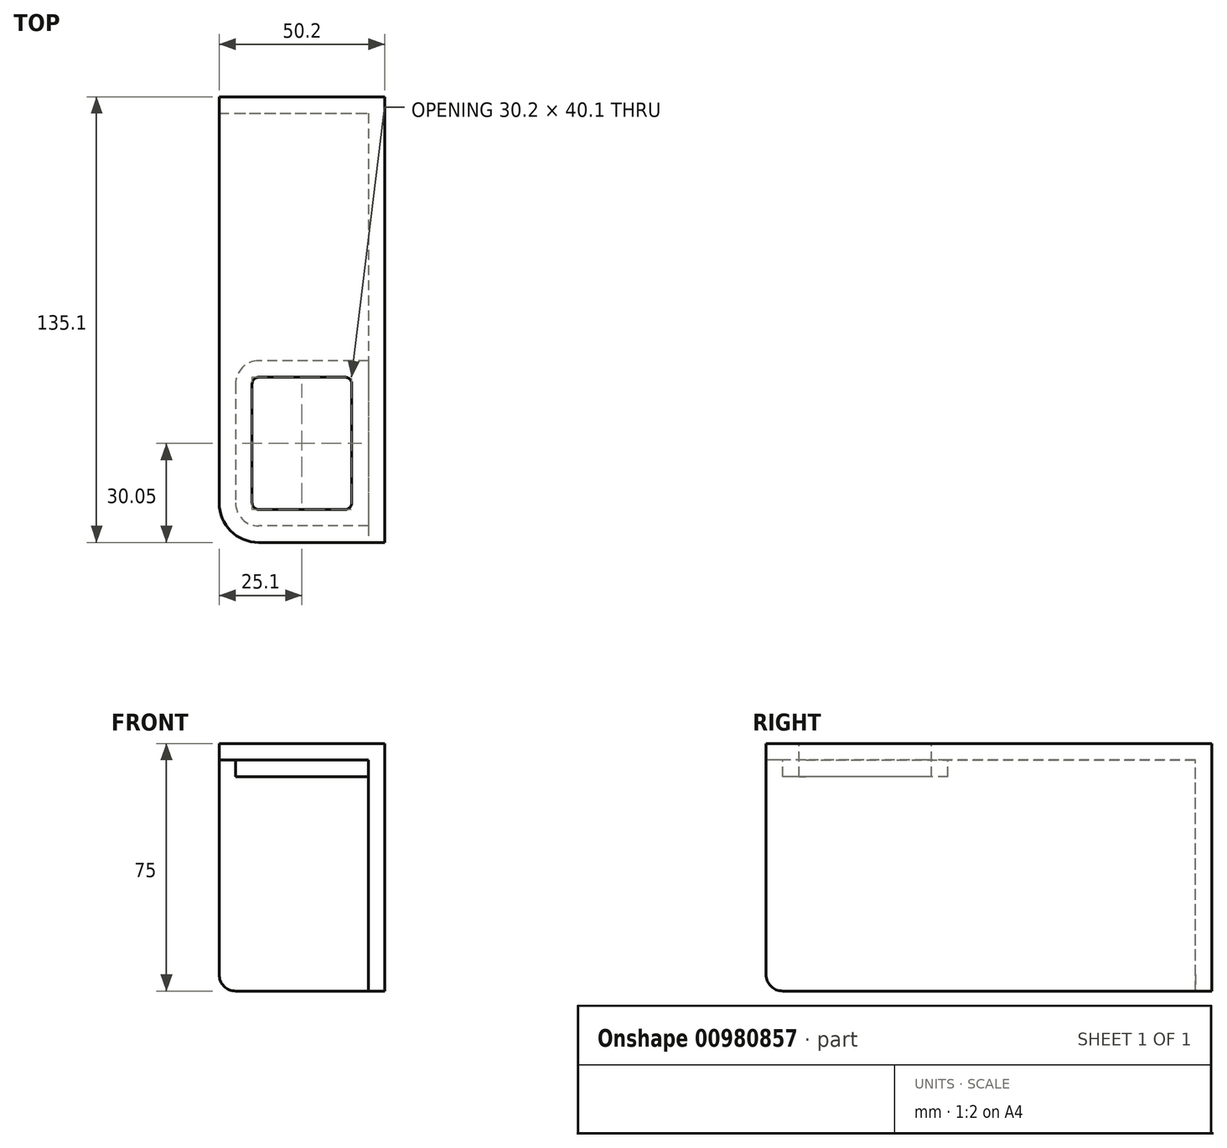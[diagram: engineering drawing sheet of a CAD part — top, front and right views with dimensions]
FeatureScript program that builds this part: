
annotation { "Feature Type Name" : "Feature", "Feature Type Description" : "" }
export const myFeature = defineFeature(function(context is Context, id is Id, definition is map)
    precondition{}
    {
        {
            var Q0;
            Q0=qCreatedBy(makeId("Top.planeOp"),FACE);
            var sketch = newSketch(context, id + "F0", { "sketchPlane" : qUnion([Q0])});
            skLineSegment(sketch, "E0.bottom", {"start": v(13.1, 20.05) * mm, "end": v(-13.1, 20.05) * mm});
            skLineSegment(sketch, "E0.top", {"start": v(13.1, -20.05) * mm, "end": v(-13.1, -20.05) * mm});
            skLineSegment(sketch, "E0.left", {"start": v(15.1, 18.05) * mm, "end": v(15.1, -18.05) * mm});
            skLineSegment(sketch, "E0.right", {"start": v(-15.1, 18.05) * mm, "end": v(-15.1, -18.05) * mm});
            skPoint(sketch, "E0.middle", {"position": v(0, 0) * mm});
            skPoint(sketch, "E1.visualSharp", {"position": v(-15.1, -20.05) * mm});
            skArc(sketch, "E1.filletArc", {"start": v(-15.1, -18.05) * mm, "mid": v(-14.51, -19.46) * mm, "end": v(-13.1, -20.05) * mm});
            skPoint(sketch, "E2.visualSharp", {"position": v(15.1, -20.05) * mm});
            skArc(sketch, "E2.filletArc", {"start": v(13.1, -20.05) * mm, "mid": v(14.51, -19.46) * mm, "end": v(15.1, -18.05) * mm});
            skPoint(sketch, "E3.visualSharp", {"position": v(15.1, 20.05) * mm});
            skArc(sketch, "E3.filletArc", {"start": v(15.1, 18.05) * mm, "mid": v(14.51, 19.46) * mm, "end": v(13.1, 20.05) * mm});
            skPoint(sketch, "E4.visualSharp", {"position": v(-15.1, 20.05) * mm});
            skArc(sketch, "E4.filletArc", {"start": v(-13.1, 20.05) * mm, "mid": v(-14.51, 19.46) * mm, "end": v(-15.1, 18.05) * mm});
            skArc(sketch, "E5.0", {"start": v(-13.1, 25.05) * mm, "mid": v(-18.05, 23) * mm, "end": v(-20.1, 18.05) * mm});
            skLineSegment(sketch, "E5.1", {"start": v(20.1, 25.05) * mm, "end": v(-13.1, 25.05) * mm});
            skLineSegment(sketch, "E5.2", {"start": v(-20.1, 18.05) * mm, "end": v(-20.1, -18.05) * mm});
            skArc(sketch, "E5.4", {"start": v(-20.1, -18.05) * mm, "mid": v(-18.05, -23) * mm, "end": v(-13.1, -25.05) * mm});
            skLineSegment(sketch, "E5.5", {"start": v(20.1, -25.05) * mm, "end": v(-13.1, -25.05) * mm});
            skLineSegment(sketch, "E6", {"start": v(-18.7, 95.35) * mm, "end": v(21.85, 95.35) * mm, "construction": true});
            skLineSegment(sketch, "E7.bottom", {"start": v(-13.1, -30.05) * mm, "end": v(25.1, -30.05) * mm});
            skLineSegment(sketch, "E7.top", {"start": v(-25.1, 105.05) * mm, "end": v(25.1, 105.05) * mm});
            skLineSegment(sketch, "E7.left", {"start": v(-25.1, -18.05) * mm, "end": v(-25.1, 105.05) * mm});
            skLineSegment(sketch, "E7.right", {"start": v(25.1, -30.05) * mm, "end": v(25.1, 105.05) * mm});
            skLineSegment(sketch, "E8", {"start": v(-25.1, 100.05) * mm, "end": v(20.1, 100.05) * mm});
            skLineSegment(sketch, "E9", {"start": v(20.1, 100.05) * mm, "end": v(20.1, -30.05) * mm});
            skPoint(sketch, "E10.visualSharp", {"position": v(-25.1, -30.05) * mm});
            skArc(sketch, "E10.filletArc", {"start": v(-25.1, -18.05) * mm, "mid": v(-21.59, -26.54) * mm, "end": v(-13.1, -30.05) * mm});
            skSolve(sketch);
        }
        {
            var Q0;
            Q0=makeQuery(id+"F0.imprint","IMPRINT",FACE,{"disambiguationData":[TD([[makeQuery(id+"F0.imprint","IMPRINT",EDGE,{"derivedFrom":sQuery(id+"F0.wireOp",EDGE,"E5.0")}),-1.0]])]});
            extrude(context, id + "F1", {"entities" : qUnion([Q0]), "oppositeDirection" : true, "depth" : 5 * mm, "offsetDistance" : 25 * mm});
        }
        {
            var Q0;
            Q0=makeQuery(id+"F0.imprint","IMPRINT",FACE,{"disambiguationData":[TD([[makeQuery(id+"F0.imprint","IMPRINT",EDGE,{"derivedFrom":sQuery(id+"F0.wireOp",EDGE,"E0.bottom")}),-1.0]])]});
            extrude(context, id + "F2", {"entities" : qUnion([Q0]), "operationType" : NewBodyOperationType.ADD, "oppositeDirection" : true, "depth" : 10 * mm, "offsetDistance" : 25 * mm});
        }
        {
            var Q0;
            {var subQ2=sQuery(id+"F0.wireOp",EDGE,"E7.top");Q0=makeQuery(id+"F0.imprint","IMPRINT",FACE,{"disambiguationData":[TD([[makeQuery(id+"F0.imprint","IMPRINT",EDGE,{"derivedFrom":subQ2}),-1.0]])]});}
            extrude(context, id + "F3", {"entities" : qUnion([Q0]), "operationType" : NewBodyOperationType.ADD, "oppositeDirection" : true, "depth" : 75 * mm, "offsetDistance" : 25 * mm});
        }
        {
            var Q0;
            {var subQ0=sQuery(id+"F0.wireOp",EDGE,"E9");Q0=makeQuery(id+"F1.opExtrude","CAP_EDGE",EDGE,{"disambiguationData":[OSD([subQ0]),TDD([makeQuery(id+"F0.imprint","IMPRINT",EDGE,{"disambiguationData":[TD([[makeQuery(id+"F0.imprint","INTERSECT",VERTEX,{"derivedFrom":[sQuery(id+"F0.wireOp",EDGE,"E5.5"),subQ0]}),-1.0]])],"derivedFrom":subQ0})])],"isStart":false});}
            var Q1;
            {var subQ0=sQuery(id+"F0.wireOp",EDGE,"E9");Q1=makeQuery(id+"F1.opExtrude","CAP_EDGE",EDGE,{"disambiguationData":[OSD([subQ0]),TDD([makeQuery(id+"F0.imprint","IMPRINT",EDGE,{"disambiguationData":[TD([[makeQuery(id+"F0.imprint","INTERSECT",VERTEX,{"derivedFrom":[sQuery(id+"F0.wireOp",EDGE,"E5.1"),subQ0]}),1.0]])],"derivedFrom":subQ0})])],"isStart":false});}
            var Q2;
            Q2=makeQuery(id+"F2.opExtrude","CAP_EDGE",EDGE,{"disambiguationData":[OSD([sQuery(id+"F0.wireOp",EDGE,"E9")])],"isStart":false});
            var Q3;
            Q3=makeQuery(id+"F3.opExtrude","CAP_EDGE",EDGE,{"disambiguationData":[OSD([sQuery(id+"F0.wireOp",EDGE,"E7.bottom")])],"isStart":false});
            var Q4;
            Q4=makeQuery(id+"F3.opExtrude","CAP_EDGE",EDGE,{"disambiguationData":[OSD([sQuery(id+"F0.wireOp",EDGE,"E7.left")])],"isStart":false});
            var Q5;
            Q5=makeQuery(id+"F1.opExtrude","CAP_EDGE",EDGE,{"disambiguationData":[OSD([sQuery(id+"F0.wireOp",EDGE,"E8")])],"isStart":false});
            fillet(context, id + "F4", {"entities" : qUnion([Q0, Q1, Q2, Q3, Q4, Q5]), "radius" : 5 * mm, "tangentPropagation" : true, "allowEdgeOverflow" : false});
        }
    });
